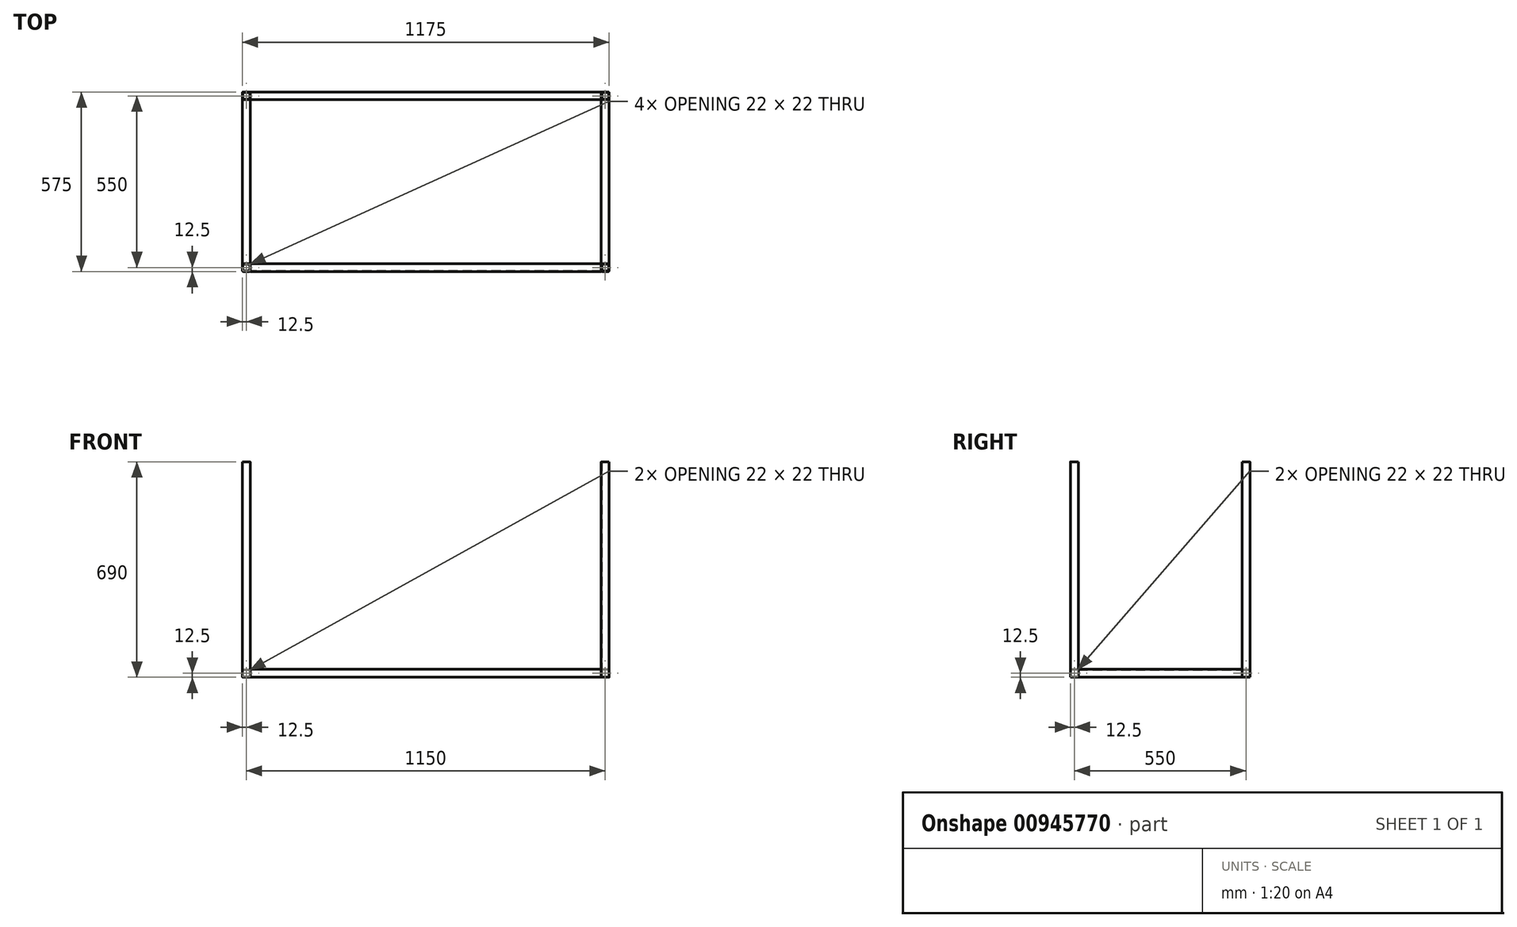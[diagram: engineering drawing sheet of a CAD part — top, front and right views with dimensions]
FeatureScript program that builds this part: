
annotation { "Feature Type Name" : "Feature", "Feature Type Description" : "" }
export const myFeature = defineFeature(function(context is Context, id is Id, definition is map)
    precondition{}
    {
        {
            assignVariable(context, id + "F0", {"variableType" : VariableType.LENGTH, "name" : "H", "lengthValue" : 690 * mm});
        }
        {
            var Q0;
            Q0=qCreatedBy(makeId("Top.planeOp"),FACE);
            var sketch = newSketch(context, id + "F1", { "sketchPlane" : qUnion([Q0])});
            skLineSegment(sketch, "E0.bottom", {"start": v(587.5, -287.5) * mm, "end": v(-587.5, -287.5) * mm, "construction": true});
            skLineSegment(sketch, "E0.top", {"start": v(587.5, 287.5) * mm, "end": v(-587.5, 287.5) * mm, "construction": true});
            skLineSegment(sketch, "E0.left", {"start": v(587.5, -287.5) * mm, "end": v(587.5, 287.5) * mm, "construction": true});
            skLineSegment(sketch, "E0.right", {"start": v(-587.5, -287.5) * mm, "end": v(-587.5, 287.5) * mm, "construction": true});
            skPoint(sketch, "E0.middle", {"position": v(0, 0) * mm});
            skLineSegment(sketch, "E1", {"start": v(-587.5, 262.5) * mm, "end": v(587.5, 262.5) * mm, "construction": true});
            skLineSegment(sketch, "E2", {"start": v(0, 287.5) * mm, "end": v(0, -287.5) * mm, "construction": true});
            skLineSegment(sketch, "E3", {"start": v(-587.5, 0) * mm, "end": v(587.5, 0) * mm, "construction": true});
            skLineSegment(sketch, "E4", {"start": v(-562.5, 287.5) * mm, "end": v(-562.5, -287.5) * mm, "construction": true});
            skLineSegment(sketch, "E5.MirrorCS", {"start": v(562.5, 287.5) * mm, "end": v(562.5, -287.5) * mm, "construction": true});
            skLineSegment(sketch, "E6.MirrorCS", {"start": v(-587.5, -262.5) * mm, "end": v(587.5, -262.5) * mm, "construction": true});
            skSolve(sketch);
        }
        {
            var Q0;
            Q0=qCreatedBy(makeId("Top.planeOp"),FACE);
            var sketch = newSketch(context, id + "F2", { "sketchPlane" : qUnion([Q0])});
            skLineSegment(sketch, "E7.bottom", {"start": v(-585.5, 287.5) * mm, "end": v(-564.5, 287.5) * mm});
            skLineSegment(sketch, "E7.top", {"start": v(-585.5, 262.5) * mm, "end": v(-564.5, 262.5) * mm});
            skLineSegment(sketch, "E7.left", {"start": v(-587.5, 285.5) * mm, "end": v(-587.5, 264.5) * mm});
            skLineSegment(sketch, "E7.right", {"start": v(-562.5, 285.5) * mm, "end": v(-562.5, 264.5) * mm});
            skPoint(sketch, "E8.visualSharp", {"position": v(-587.5, 287.5) * mm});
            skArc(sketch, "E8.filletArc", {"start": v(-585.5, 287.5) * mm, "mid": v(-586.91, 286.91) * mm, "end": v(-587.5, 285.5) * mm});
            skPoint(sketch, "E9.visualSharp", {"position": v(-562.5, 287.5) * mm});
            skArc(sketch, "E9.filletArc", {"start": v(-562.5, 285.5) * mm, "mid": v(-563.09, 286.91) * mm, "end": v(-564.5, 287.5) * mm});
            skPoint(sketch, "E10.visualSharp", {"position": v(-562.5, 262.5) * mm});
            skArc(sketch, "E10.filletArc", {"start": v(-564.5, 262.5) * mm, "mid": v(-563.09, 263.09) * mm, "end": v(-562.5, 264.5) * mm});
            skPoint(sketch, "E11.visualSharp", {"position": v(-587.5, 262.5) * mm});
            skArc(sketch, "E11.filletArc", {"start": v(-587.5, 264.5) * mm, "mid": v(-586.91, 263.09) * mm, "end": v(-585.5, 262.5) * mm});
            skLineSegment(sketch, "E12.0", {"start": v(-585.5, 286) * mm, "end": v(-564.5, 286) * mm});
            skArc(sketch, "E13.0", {"start": v(-564, 285.5) * mm, "mid": v(-564.15, 285.85) * mm, "end": v(-564.5, 286) * mm});
            skLineSegment(sketch, "E14.0", {"start": v(-564, 285.5) * mm, "end": v(-564, 264.5) * mm});
            skArc(sketch, "E15.0", {"start": v(-564.5, 264) * mm, "mid": v(-564.15, 264.15) * mm, "end": v(-564, 264.5) * mm});
            skLineSegment(sketch, "E16.0", {"start": v(-585.5, 264) * mm, "end": v(-564.5, 264) * mm});
            skArc(sketch, "E17.0", {"start": v(-586, 264.5) * mm, "mid": v(-585.85, 264.15) * mm, "end": v(-585.5, 264) * mm});
            skLineSegment(sketch, "E18.0", {"start": v(-586, 285.5) * mm, "end": v(-586, 264.5) * mm});
            skArc(sketch, "E19.0", {"start": v(-585.5, 286) * mm, "mid": v(-585.85, 285.85) * mm, "end": v(-586, 285.5) * mm});
            skSolve(sketch);
        }
        {
            var Q0;
            Q0=makeQuery(id+"F2.imprint","IMPRINT",FACE,{"disambiguationData":[TD([[makeQuery(id+"F2.imprint","IMPRINT",EDGE,{"derivedFrom":sQuery(id+"F2.wireOp",EDGE,"E7.bottom")}),-1.0]])]});
            extrude(context, id + "F3", {"entities" : qUnion([Q0]), "depth" : getVariable(context, 'H'), "offsetDistance" : 25 * mm});
        }
        {
            var Q0;
            Q0=makeQuery(id+"F3.opExtrude","SWEPT_FACE",FACE,{"disambiguationData":[OSD([sQuery(id+"F2.wireOp",EDGE,"E7.right")])]});
            var sketch = newSketch(context, id + "F4", { "sketchPlane" : qUnion([Q0])});
            skLineSegment(sketch, "E20.bottom", {"start": v(264.5, 25) * mm, "end": v(285.5, 25) * mm});
            skLineSegment(sketch, "E20.top", {"start": v(264.5, 0) * mm, "end": v(285.5, 0) * mm});
            skLineSegment(sketch, "E20.left", {"start": v(262.5, 23) * mm, "end": v(262.5, 2) * mm});
            skLineSegment(sketch, "E20.right", {"start": v(287.5, 23) * mm, "end": v(287.5, 2) * mm});
            skPoint(sketch, "E21.visualSharp", {"position": v(262.5, 25) * mm});
            skArc(sketch, "E21.filletArc", {"start": v(264.5, 25) * mm, "mid": v(263.09, 24.41) * mm, "end": v(262.5, 23) * mm});
            skPoint(sketch, "E22.visualSharp", {"position": v(287.5, 25) * mm});
            skArc(sketch, "E22.filletArc", {"start": v(287.5, 23) * mm, "mid": v(286.91, 24.41) * mm, "end": v(285.5, 25) * mm});
            skPoint(sketch, "E23.visualSharp", {"position": v(287.5, 0) * mm});
            skArc(sketch, "E23.filletArc", {"start": v(285.5, 0) * mm, "mid": v(286.91, 0.59) * mm, "end": v(287.5, 2) * mm});
            skPoint(sketch, "E24.visualSharp", {"position": v(262.5, 0) * mm});
            skArc(sketch, "E24.filletArc", {"start": v(262.5, 2) * mm, "mid": v(263.09, 0.59) * mm, "end": v(264.5, 0) * mm});
            skLineSegment(sketch, "E25.0", {"start": v(264.5, 23.5) * mm, "end": v(285.5, 23.5) * mm});
            skArc(sketch, "E26.0", {"start": v(286, 23) * mm, "mid": v(285.85, 23.35) * mm, "end": v(285.5, 23.5) * mm});
            skLineSegment(sketch, "E27.0", {"start": v(286, 23) * mm, "end": v(286, 2) * mm});
            skArc(sketch, "E28.0", {"start": v(285.5, 1.5) * mm, "mid": v(285.85, 1.65) * mm, "end": v(286, 2) * mm});
            skLineSegment(sketch, "E29.0", {"start": v(264.5, 1.5) * mm, "end": v(285.5, 1.5) * mm});
            skArc(sketch, "E30.0", {"start": v(264, 2) * mm, "mid": v(264.15, 1.65) * mm, "end": v(264.5, 1.5) * mm});
            skLineSegment(sketch, "E31.0", {"start": v(264, 23) * mm, "end": v(264, 2) * mm});
            skArc(sketch, "E32.0", {"start": v(264.5, 23.5) * mm, "mid": v(264.15, 23.35) * mm, "end": v(264, 23) * mm});
            skSolve(sketch);
        }
        {
            var Q0;
            Q0 = qSketchRegion(id + "F4", true);
            var Q1;
            Q1=sQuery(id+"F1.wireOp",VERTEX,"E5.MirrorCS.start");
            extrude(context, id + "F5", {"entities" : qUnion([Q0]), "endBound" : BoundingType.UP_TO_VERTEX, "depth" : 25 * mm, "endBoundEntityVertex" : qUnion([Q1]), "offsetDistance" : 25 * mm});
        }
        {
            var Q0;
            Q0=makeQuery(id+"F3.opExtrude","SWEPT_FACE",FACE,{"disambiguationData":[OSD([sQuery(id+"F2.wireOp",EDGE,"E7.top")])]});
            var sketch = newSketch(context, id + "F6", { "sketchPlane" : qUnion([Q0])});
            skLineSegment(sketch, "E33.bottom", {"start": v(-585.5, 25) * mm, "end": v(-564.5, 25) * mm});
            skLineSegment(sketch, "E33.top", {"start": v(-585.5, 0) * mm, "end": v(-564.5, 0) * mm});
            skLineSegment(sketch, "E33.left", {"start": v(-587.5, 23) * mm, "end": v(-587.5, 2) * mm});
            skLineSegment(sketch, "E33.right", {"start": v(-562.5, 23) * mm, "end": v(-562.5, 2) * mm});
            skPoint(sketch, "E34.visualSharp", {"position": v(-587.5, 25) * mm});
            skArc(sketch, "E34.filletArc", {"start": v(-585.5, 25) * mm, "mid": v(-586.91, 24.41) * mm, "end": v(-587.5, 23) * mm});
            skPoint(sketch, "E35.visualSharp", {"position": v(-562.5, 25) * mm});
            skArc(sketch, "E35.filletArc", {"start": v(-562.5, 23) * mm, "mid": v(-563.09, 24.41) * mm, "end": v(-564.5, 25) * mm});
            skPoint(sketch, "E36.visualSharp", {"position": v(-562.5, 0) * mm});
            skArc(sketch, "E36.filletArc", {"start": v(-564.5, 0) * mm, "mid": v(-563.09, 0.59) * mm, "end": v(-562.5, 2) * mm});
            skPoint(sketch, "E37.visualSharp", {"position": v(-587.5, 0) * mm});
            skArc(sketch, "E37.filletArc", {"start": v(-587.5, 2) * mm, "mid": v(-586.91, 0.59) * mm, "end": v(-585.5, 0) * mm});
            skLineSegment(sketch, "E38.0", {"start": v(-585.5, 23.5) * mm, "end": v(-564.5, 23.5) * mm});
            skArc(sketch, "E39.0", {"start": v(-564, 23) * mm, "mid": v(-564.15, 23.35) * mm, "end": v(-564.5, 23.5) * mm});
            skLineSegment(sketch, "E40.0", {"start": v(-564, 23) * mm, "end": v(-564, 2) * mm});
            skArc(sketch, "E41.0", {"start": v(-564.5, 1.5) * mm, "mid": v(-564.15, 1.65) * mm, "end": v(-564, 2) * mm});
            skLineSegment(sketch, "E42.0", {"start": v(-585.5, 1.5) * mm, "end": v(-564.5, 1.5) * mm});
            skArc(sketch, "E43.0", {"start": v(-586, 2) * mm, "mid": v(-585.85, 1.65) * mm, "end": v(-585.5, 1.5) * mm});
            skLineSegment(sketch, "E44.0", {"start": v(-586, 23) * mm, "end": v(-586, 2) * mm});
            skArc(sketch, "E45.0", {"start": v(-585.5, 23.5) * mm, "mid": v(-585.85, 23.35) * mm, "end": v(-586, 23) * mm});
            skSolve(sketch);
        }
        {
            var Q0;
            Q0 = qSketchRegion(id + "F6", true);
            var Q1;
            Q1=sQuery(id+"F1.wireOp",VERTEX,"E6.MirrorCS.start");
            extrude(context, id + "F7", {"entities" : qUnion([Q0]), "endBound" : BoundingType.UP_TO_VERTEX, "depth" : 25 * mm, "endBoundEntityVertex" : qUnion([Q1]), "offsetDistance" : 25 * mm});
        }
        {
            var Q0;
            Q0=makeQuery(id+"F3.opExtrude","SWEPT_BODY",BODY,{"disambiguationData":[OSD([sQuery(id+"F2.wireOp",EDGE,"E7.bottom"),sQuery(id+"F2.wireOp",EDGE,"E7.top"),sQuery(id+"F2.wireOp",EDGE,"E7.left"),sQuery(id+"F2.wireOp",EDGE,"E7.right"),sQuery(id+"F2.wireOp",EDGE,"E8.filletArc"),sQuery(id+"F2.wireOp",EDGE,"E9.filletArc"),sQuery(id+"F2.wireOp",EDGE,"E10.filletArc"),sQuery(id+"F2.wireOp",EDGE,"E11.filletArc"),sQuery(id+"F2.wireOp",EDGE,"E12.0"),sQuery(id+"F2.wireOp",EDGE,"E13.0"),sQuery(id+"F2.wireOp",EDGE,"E14.0"),sQuery(id+"F2.wireOp",EDGE,"E15.0"),sQuery(id+"F2.wireOp",EDGE,"E16.0"),sQuery(id+"F2.wireOp",EDGE,"E17.0"),sQuery(id+"F2.wireOp",EDGE,"E18.0"),sQuery(id+"F2.wireOp",EDGE,"E19.0")])]});
            var Q1;
            Q1=makeQuery(id+"F7.opExtrude","SWEPT_BODY",BODY,{"disambiguationData":[OSD([sQuery(id+"F6.wireOp",EDGE,"E33.bottom"),sQuery(id+"F6.wireOp",EDGE,"E33.top"),sQuery(id+"F6.wireOp",EDGE,"E33.left"),sQuery(id+"F6.wireOp",EDGE,"E33.right"),sQuery(id+"F6.wireOp",EDGE,"E34.filletArc"),sQuery(id+"F6.wireOp",EDGE,"E35.filletArc"),sQuery(id+"F6.wireOp",EDGE,"E36.filletArc"),sQuery(id+"F6.wireOp",EDGE,"E37.filletArc"),sQuery(id+"F6.wireOp",EDGE,"E38.0"),sQuery(id+"F6.wireOp",EDGE,"E39.0"),sQuery(id+"F6.wireOp",EDGE,"E40.0"),sQuery(id+"F6.wireOp",EDGE,"E41.0"),sQuery(id+"F6.wireOp",EDGE,"E42.0"),sQuery(id+"F6.wireOp",EDGE,"E43.0"),sQuery(id+"F6.wireOp",EDGE,"E44.0"),sQuery(id+"F6.wireOp",EDGE,"E45.0")])]});
            var Q2;
            Q2=qCreatedBy(makeId("Right.planeOp"),FACE);
            mirror(context, id + "F8", {"entities" : qUnion([Q0, Q1]), "mirrorPlane" : qUnion([Q2])});
        }
        {
            var Q0;
            Q0=makeQuery(id+"F5.opExtrude","SWEPT_BODY",BODY,{"disambiguationData":[OSD([sQuery(id+"F4.wireOp",EDGE,"E20.bottom"),sQuery(id+"F4.wireOp",EDGE,"E20.top"),sQuery(id+"F4.wireOp",EDGE,"E20.left"),sQuery(id+"F4.wireOp",EDGE,"E20.right"),sQuery(id+"F4.wireOp",EDGE,"E21.filletArc"),sQuery(id+"F4.wireOp",EDGE,"E22.filletArc"),sQuery(id+"F4.wireOp",EDGE,"E23.filletArc"),sQuery(id+"F4.wireOp",EDGE,"E24.filletArc"),sQuery(id+"F4.wireOp",EDGE,"E25.0"),sQuery(id+"F4.wireOp",EDGE,"E26.0"),sQuery(id+"F4.wireOp",EDGE,"E27.0"),sQuery(id+"F4.wireOp",EDGE,"E28.0"),sQuery(id+"F4.wireOp",EDGE,"E29.0"),sQuery(id+"F4.wireOp",EDGE,"E30.0"),sQuery(id+"F4.wireOp",EDGE,"E31.0"),sQuery(id+"F4.wireOp",EDGE,"E32.0")])]});
            var Q1;
            Q1=makeQuery(id+"F3.opExtrude","SWEPT_BODY",BODY,{"disambiguationData":[OSD([sQuery(id+"F2.wireOp",EDGE,"E7.bottom"),sQuery(id+"F2.wireOp",EDGE,"E7.top"),sQuery(id+"F2.wireOp",EDGE,"E7.left"),sQuery(id+"F2.wireOp",EDGE,"E7.right"),sQuery(id+"F2.wireOp",EDGE,"E8.filletArc"),sQuery(id+"F2.wireOp",EDGE,"E9.filletArc"),sQuery(id+"F2.wireOp",EDGE,"E10.filletArc"),sQuery(id+"F2.wireOp",EDGE,"E11.filletArc"),sQuery(id+"F2.wireOp",EDGE,"E12.0"),sQuery(id+"F2.wireOp",EDGE,"E13.0"),sQuery(id+"F2.wireOp",EDGE,"E14.0"),sQuery(id+"F2.wireOp",EDGE,"E15.0"),sQuery(id+"F2.wireOp",EDGE,"E16.0"),sQuery(id+"F2.wireOp",EDGE,"E17.0"),sQuery(id+"F2.wireOp",EDGE,"E18.0"),sQuery(id+"F2.wireOp",EDGE,"E19.0")])]});
            var Q2;
            Q2=makeQuery(id+"F8.opPattern","COPY",BODY,{"derivedFrom":makeQuery(id+"F3.opExtrude","SWEPT_BODY",BODY,{"disambiguationData":[OSD([sQuery(id+"F2.wireOp",EDGE,"E7.bottom"),sQuery(id+"F2.wireOp",EDGE,"E7.top"),sQuery(id+"F2.wireOp",EDGE,"E7.left"),sQuery(id+"F2.wireOp",EDGE,"E7.right"),sQuery(id+"F2.wireOp",EDGE,"E8.filletArc"),sQuery(id+"F2.wireOp",EDGE,"E9.filletArc"),sQuery(id+"F2.wireOp",EDGE,"E10.filletArc"),sQuery(id+"F2.wireOp",EDGE,"E11.filletArc"),sQuery(id+"F2.wireOp",EDGE,"E12.0"),sQuery(id+"F2.wireOp",EDGE,"E13.0"),sQuery(id+"F2.wireOp",EDGE,"E14.0"),sQuery(id+"F2.wireOp",EDGE,"E15.0"),sQuery(id+"F2.wireOp",EDGE,"E16.0"),sQuery(id+"F2.wireOp",EDGE,"E17.0"),sQuery(id+"F2.wireOp",EDGE,"E18.0"),sQuery(id+"F2.wireOp",EDGE,"E19.0")])]}),"instanceName":"1"});
            var Q3;
            Q3=qCreatedBy(makeId("Front.planeOp"),FACE);
            mirror(context, id + "F9", {"entities" : qUnion([Q0, Q1, Q2]), "mirrorPlane" : qUnion([Q3])});
        }
    });
